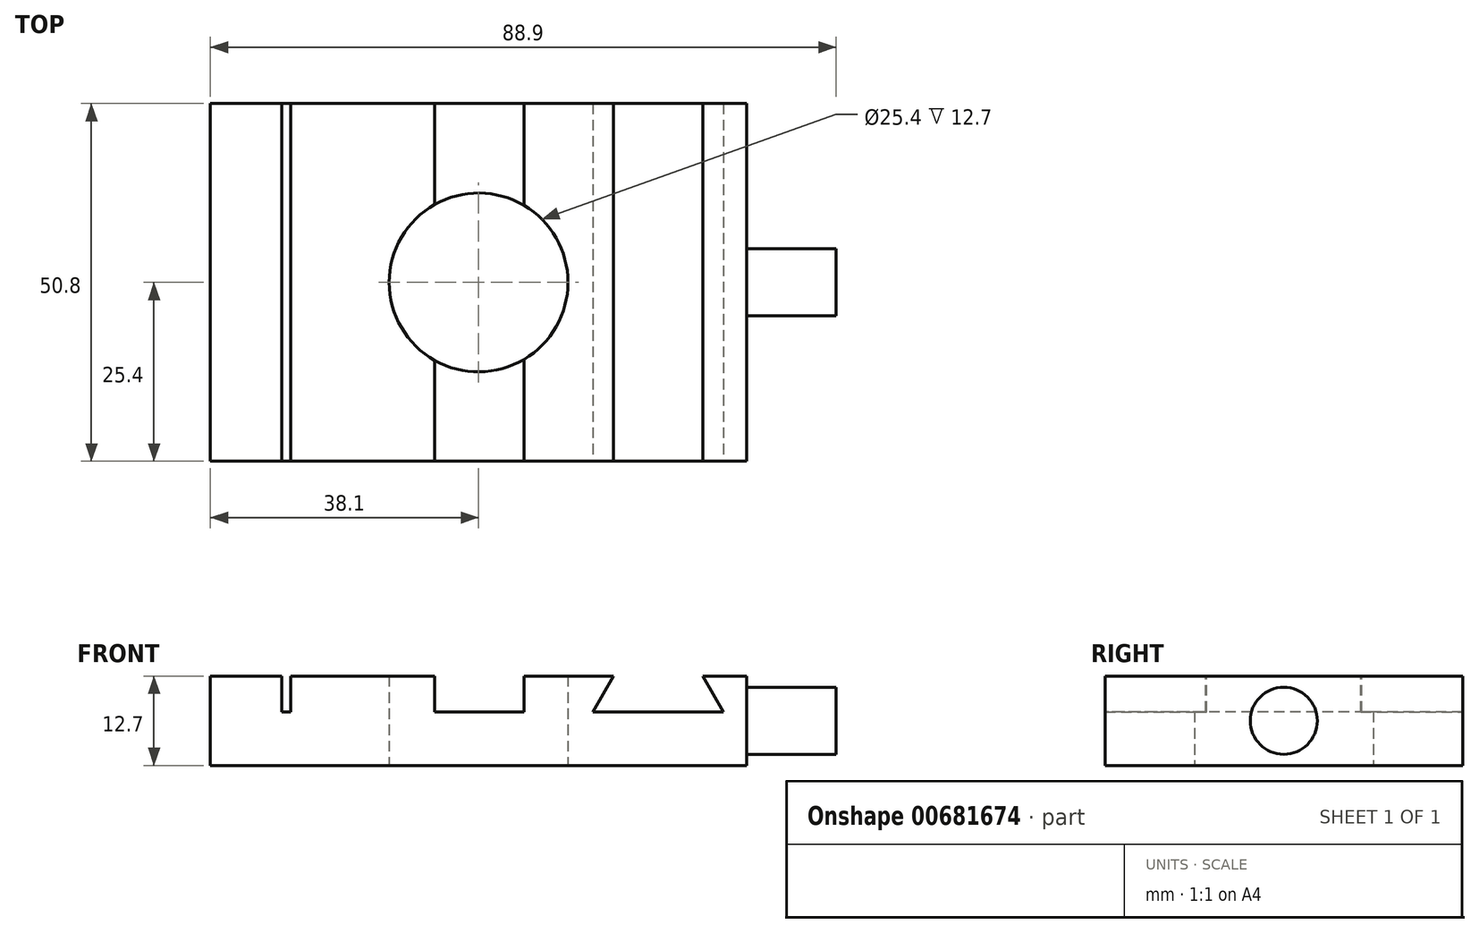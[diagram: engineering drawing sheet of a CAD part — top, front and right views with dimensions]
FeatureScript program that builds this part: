
annotation { "Feature Type Name" : "Feature", "Feature Type Description" : "" }
export const myFeature = defineFeature(function(context is Context, id is Id, definition is map)
    precondition{}
    {
        {
            var Q0;
            Q0=qCreatedBy(makeId("Top.planeOp"),FACE);
            var sketch = newSketch(context, id + "F0", { "sketchPlane" : qUnion([Q0])});
            skLineSegment(sketch, "E0.bottom", {"start": v(38.1, -25.4) * mm, "end": v(-38.1, -25.4) * mm});
            skLineSegment(sketch, "E0.top", {"start": v(38.1, 25.4) * mm, "end": v(-38.1, 25.4) * mm});
            skLineSegment(sketch, "E0.left", {"start": v(38.1, -25.4) * mm, "end": v(38.1, 25.4) * mm});
            skLineSegment(sketch, "E0.right", {"start": v(-38.1, -25.4) * mm, "end": v(-38.1, 25.4) * mm});
            skPoint(sketch, "E0.middle", {"position": v(0, 0) * mm});
            skCircle(sketch, "E1", {"center": v(0, 0) * mm, "radius": 12.7 * mm});
            skSolve(sketch);
        }
        {
            var Q0;
            Q0=makeQuery(id+"F0.imprint","IMPRINT",FACE,{"disambiguationData":[TD([[makeQuery(id+"F0.imprint","IMPRINT",EDGE,{"derivedFrom":sQuery(id+"F0.wireOp",EDGE,"E0.bottom")}),-1.0]])]});
            extrude(context, id + "F1", {"entities" : qUnion([Q0]), "depth" : 12.7 * mm, "offsetDistance" : 25 * mm});
        }
        {
            var Q0;
            Q0=makeQuery(id+"F1.opExtrude","CAP_FACE",FACE,{"disambiguationData":[OSD([sQuery(id+"F0.wireOp",EDGE,"E0.bottom"),sQuery(id+"F0.wireOp",EDGE,"E0.top"),sQuery(id+"F0.wireOp",EDGE,"E0.left"),sQuery(id+"F0.wireOp",EDGE,"E0.right"),sQuery(id+"F0.wireOp",EDGE,"E1")])],"isStart":false});
            var sketch = newSketch(context, id + "F2", { "sketchPlane" : qUnion([Q0])});
            skLineSegment(sketch, "E2.bottom", {"start": v(-27.94, 25.4) * mm, "end": v(-26.67, 25.4) * mm});
            skLineSegment(sketch, "E2.top", {"start": v(-27.94, -25.4) * mm, "end": v(-26.67, -25.4) * mm});
            skLineSegment(sketch, "E2.left", {"start": v(-27.94, 25.4) * mm, "end": v(-27.94, -25.4) * mm});
            skLineSegment(sketch, "E2.right", {"start": v(-26.67, 25.4) * mm, "end": v(-26.67, -25.4) * mm});
            skLineSegment(sketch, "E3", {"start": v(-6.24, 25.4) * mm, "end": v(-6.24, -25.4) * mm});
            skLineSegment(sketch, "E4", {"start": v(-6.24, -25.4) * mm, "end": v(6.46, -25.4) * mm});
            skLineSegment(sketch, "E5", {"start": v(6.46, -25.4) * mm, "end": v(6.46, 25.4) * mm});
            skPoint(sketch, "E6", {"position": v(0, 0) * mm});
            skLineSegment(sketch, "E7", {"start": v(0, 25.4) * mm, "end": v(0, -25.4) * mm, "construction": true});
            skSolve(sketch);
        }
        {
            var Q0;
            Q0=makeQuery(id+"F2.imprint","IMPRINT",FACE,{"disambiguationData":[TD([[makeQuery(id+"F2.imprint","IMPRINT",EDGE,{"derivedFrom":sQuery(id+"F2.wireOp",EDGE,"E2.bottom")}),1.0]])]});
            var Q1;
            {var subQ0=sQuery(id+"F2.wireOp",EDGE,"E3");var subQ1=makeQuery(id+"F1.opExtrude","CAP_EDGE",EDGE,{"disambiguationData":[OSD([sQuery(id+"F0.wireOp",EDGE,"E0.top")])],"isStart":false});var subQ2=makeQuery(id+"F2.imprint","INTERSECT",VERTEX,{"derivedFrom":[subQ1,subQ0]});Q1=makeQuery(id+"F2.imprint","IMPRINT",FACE,{"disambiguationData":[TD([[makeQuery(id+"F2.imprint","IMPRINT",EDGE,{"disambiguationData":[TD([[subQ2,-1.0]])],"derivedFrom":subQ0}),1.0]])]});}
            var Q2;
            {var subQ0=sQuery(id+"F2.wireOp",EDGE,"E4");Q2=makeQuery(id+"F2.imprint","IMPRINT",FACE,{"disambiguationData":[TD([[makeQuery(id+"F2.imprint","IMPRINT",EDGE,{"derivedFrom":subQ0}),-1.0]])]});}
            extrude(context, id + "F3", {"entities" : qUnion([Q0, Q1, Q2]), "operationType" : NewBodyOperationType.REMOVE, "oppositeDirection" : true, "depth" : 5.08 * mm, "offsetDistance" : 25.4 * mm});
        }
        {
            var Q0;
            Q0=makeQuery(id+"F1.opExtrude","SWEPT_FACE",FACE,{"disambiguationData":[OSD([sQuery(id+"F0.wireOp",EDGE,"E0.bottom")])]});
            var sketch = newSketch(context, id + "F4", { "sketchPlane" : qUnion([Q0])});
            skLineSegment(sketch, "E8", {"start": v(19.16, 12.7) * mm, "end": v(16.23, 7.62) * mm});
            skLineSegment(sketch, "E9", {"start": v(16.23, 7.62) * mm, "end": v(34.8, 7.62) * mm});
            skLineSegment(sketch, "E10", {"start": v(34.8, 7.62) * mm, "end": v(31.86, 12.7) * mm});
            skLineSegment(sketch, "E11", {"start": v(31.86, 12.7) * mm, "end": v(19.16, 12.7) * mm});
            skLineSegment(sketch, "E12", {"start": v(25.51, 7.62) * mm, "end": v(25.51, 12.7) * mm, "construction": true});
            skSolve(sketch);
        }
        {
            var Q0;
            Q0=makeQuery(id+"F4.imprint","IMPRINT",FACE,{"disambiguationData":[TD([[makeQuery(id+"F4.imprint","IMPRINT",EDGE,{"derivedFrom":sQuery(id+"F4.wireOp",EDGE,"E8")}),1.0]])]});
            extrude(context, id + "F5", {"entities" : qUnion([Q0]), "operationType" : NewBodyOperationType.REMOVE, "endBound" : BoundingType.THROUGH_ALL, "oppositeDirection" : true, "depth" : 25.4 * mm, "offsetDistance" : 25.4 * mm});
        }
        {
            var Q0;
            Q0=makeQuery(id+"F1.opExtrude","SWEPT_FACE",FACE,{"disambiguationData":[OSD([sQuery(id+"F0.wireOp",EDGE,"E0.left")])]});
            var sketch = newSketch(context, id + "F6", { "sketchPlane" : qUnion([Q0])});
            skCircle(sketch, "E13", {"center": v(0, 6.35) * mm, "radius": 4.76 * mm});
            skPoint(sketch, "E13.centerSnap0", {"position": v(0, 12.7) * mm});
            skPoint(sketch, "E13.centerSnap1", {"position": v(-25.4, 6.35) * mm});
            skSolve(sketch);
        }
        {
            var Q0;
            Q0=makeQuery(id+"F6.imprint","IMPRINT",FACE,{"disambiguationData":[TD([[makeQuery(id+"F6.imprint","IMPRINT",EDGE,{"derivedFrom":sQuery(id+"F6.wireOp",EDGE,"E13")}),1.0]])]});
            extrude(context, id + "F7", {"entities" : qUnion([Q0]), "operationType" : NewBodyOperationType.ADD, "depth" : 12.7 * mm, "offsetDistance" : 25.4 * mm});
        }
    });
